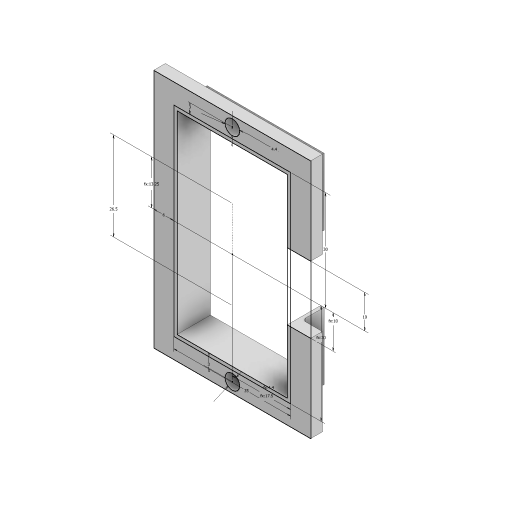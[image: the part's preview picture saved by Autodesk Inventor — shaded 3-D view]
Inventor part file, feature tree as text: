
AUTODESK INVENTOR PART (.ipt)
format: ipt  version: 2023 (Build 270158000, 158)  size: 145,408 bytes
history: native  units: mm
features: extrude x3, sketch x1, fillet x1
ambient origin geometry x8: Origin, YZ Plane, XZ Plane, XY Plane, X Axis, Y Axis, Z Axis, Center Point
bodies: Body1 (feature_tree)
feature tree (5):
  sketch  "Sketch1"  dims[d2=26.5mm d3=13.25mm d13=35.0mm d14=17.5mm d15=30.0mm d16=30.0mm d17=6.0mm d22=1.0mm d23=4.4mm d24=3.0mm d26=4.4mm d27=3.0mm d28=10.0mm d29=10.0mm d30=3.5mm d31=0.0mm d32=10.0mm d33=0.0mm d34=0.0mm d35=-0.872665mm d36=1.0mm]
  extrude  "Extrusion3"  Depth=1.0mm
  extrude  "Extrusion4"  Depth=35.0mm
  extrude  "Extrusion5"  Depth=1.0mm
  fillet  "Fillet1"  Radius=30.0mm
